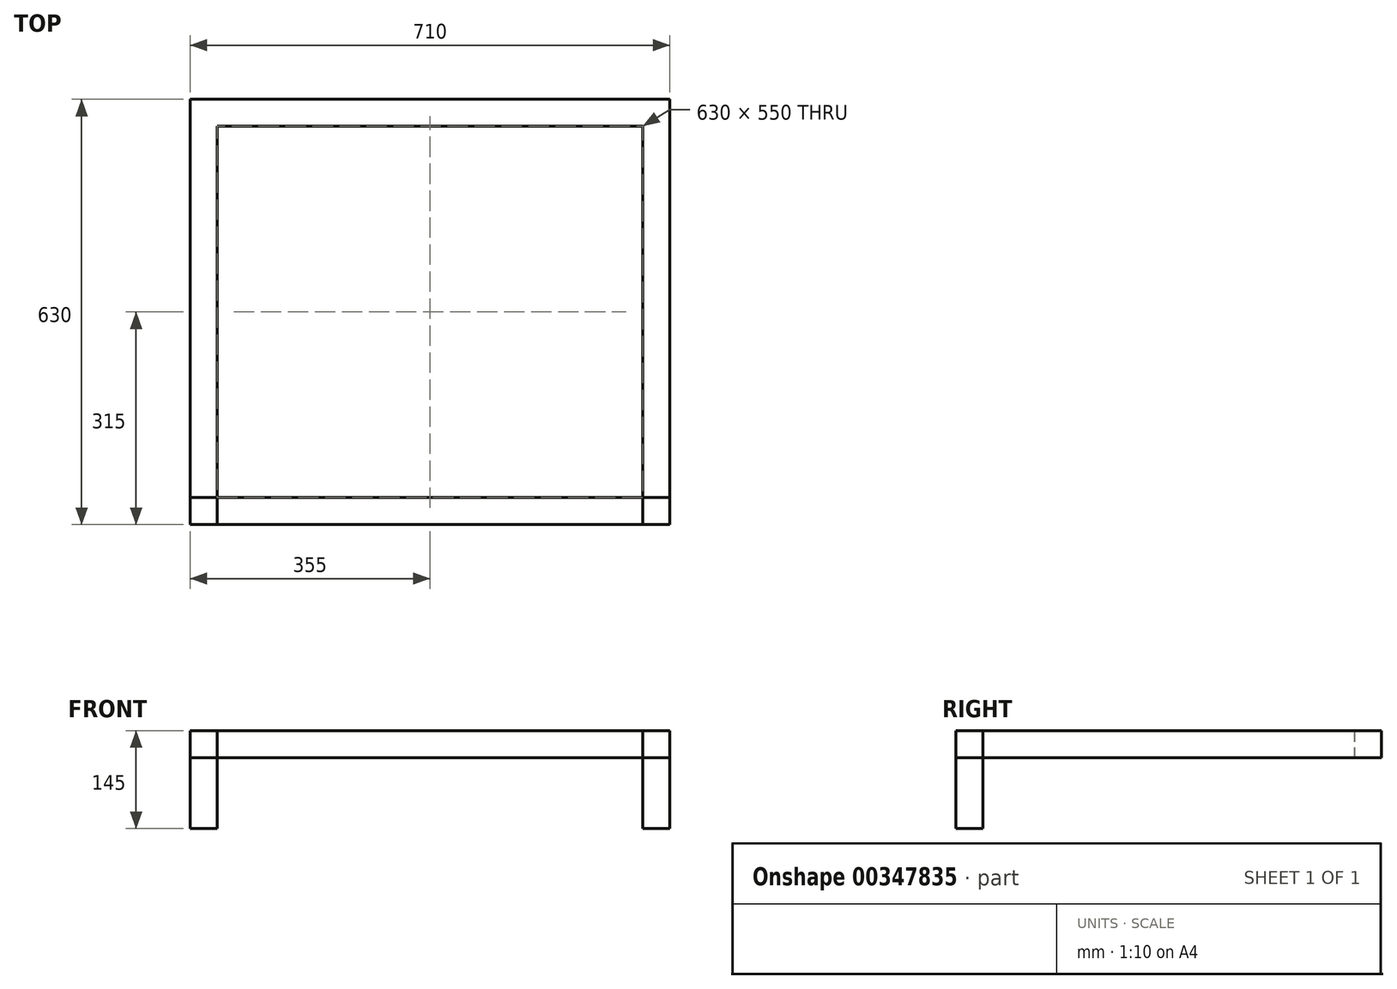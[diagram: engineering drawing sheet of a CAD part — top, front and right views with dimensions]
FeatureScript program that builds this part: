
annotation { "Feature Type Name" : "Feature", "Feature Type Description" : "" }
export const myFeature = defineFeature(function(context is Context, id is Id, definition is map)
    precondition{}
    {
        {
            var Q0;
            Q0=qCreatedBy(makeId("Top.planeOp"),FACE);
            var sketch = newSketch(context, id + "F0", { "sketchPlane" : qUnion([Q0])});
            skLineSegment(sketch, "E0.bottom", {"start": v(355, -315) * mm, "end": v(-355, -315) * mm});
            skLineSegment(sketch, "E0.top", {"start": v(355, 315) * mm, "end": v(-355, 315) * mm});
            skLineSegment(sketch, "E0.left", {"start": v(355, -315) * mm, "end": v(355, 315) * mm});
            skLineSegment(sketch, "E0.right", {"start": v(-355, -315) * mm, "end": v(-355, 315) * mm});
            skPoint(sketch, "E0.middle", {"position": v(0, 0) * mm});
            skLineSegment(sketch, "E1.0", {"start": v(315, 275) * mm, "end": v(-315, 275) * mm});
            skLineSegment(sketch, "E1.1", {"start": v(315, -275) * mm, "end": v(315, 275) * mm});
            skLineSegment(sketch, "E1.2", {"start": v(315, -275) * mm, "end": v(-315, -275) * mm});
            skLineSegment(sketch, "E1.3", {"start": v(-315, -275) * mm, "end": v(-315, 275) * mm});
            skLineSegment(sketch, "E2.bottom", {"start": v(-355, 315) * mm, "end": v(-315, 315) * mm});
            skLineSegment(sketch, "E2.top", {"start": v(-355, 275) * mm, "end": v(-315, 275) * mm});
            skLineSegment(sketch, "E2.left", {"start": v(-355, 315) * mm, "end": v(-355, 275) * mm});
            skLineSegment(sketch, "E2.right", {"start": v(-315, 315) * mm, "end": v(-315, 275) * mm});
            skLineSegment(sketch, "E3.bottom", {"start": v(355, 315) * mm, "end": v(315, 315) * mm});
            skLineSegment(sketch, "E3.top", {"start": v(355, 275) * mm, "end": v(315, 275) * mm});
            skLineSegment(sketch, "E3.left", {"start": v(355, 315) * mm, "end": v(355, 275) * mm});
            skLineSegment(sketch, "E3.right", {"start": v(315, 315) * mm, "end": v(315, 275) * mm});
            skLineSegment(sketch, "E4.bottom", {"start": v(315, -275) * mm, "end": v(355, -275) * mm});
            skLineSegment(sketch, "E4.top", {"start": v(315, -315) * mm, "end": v(355, -315) * mm});
            skLineSegment(sketch, "E4.left", {"start": v(315, -275) * mm, "end": v(315, -315) * mm});
            skLineSegment(sketch, "E4.right", {"start": v(355, -275) * mm, "end": v(355, -315) * mm});
            skLineSegment(sketch, "E5.bottom", {"start": v(-315, -275) * mm, "end": v(-355, -275) * mm});
            skLineSegment(sketch, "E5.top", {"start": v(-315, -315) * mm, "end": v(-355, -315) * mm});
            skLineSegment(sketch, "E5.left", {"start": v(-315, -275) * mm, "end": v(-315, -315) * mm});
            skLineSegment(sketch, "E5.right", {"start": v(-355, -275) * mm, "end": v(-355, -315) * mm});
            skSolve(sketch);
        }
        {
            var Q0;
            Q0=makeQuery(id+"F0.imprint","IMPRINT",FACE,{"disambiguationData":[TD([[makeQuery(id+"F0.imprint","IMPRINT",EDGE,{"derivedFrom":sQuery(id+"F0.wireOp",EDGE,"E2.bottom")}),-1.0]])]});
            var Q1;
            Q1=makeQuery(id+"F0.imprint","IMPRINT",FACE,{"disambiguationData":[TD([[makeQuery(id+"F0.imprint","IMPRINT",EDGE,{"derivedFrom":sQuery(id+"F0.wireOp",EDGE,"E3.bottom")}),1.0]])]});
            var Q2;
            Q2=makeQuery(id+"F0.imprint","IMPRINT",FACE,{"disambiguationData":[TD([[makeQuery(id+"F0.imprint","IMPRINT",EDGE,{"derivedFrom":sQuery(id+"F0.wireOp",EDGE,"E4.bottom")}),-1.0]])]});
            var Q3;
            Q3=makeQuery(id+"F0.imprint","IMPRINT",FACE,{"disambiguationData":[TD([[makeQuery(id+"F0.imprint","IMPRINT",EDGE,{"derivedFrom":sQuery(id+"F0.wireOp",EDGE,"E5.bottom")}),1.0]])]});
            extrude(context, id + "F1", {"entities" : qUnion([Q0, Q1, Q2, Q3]), "oppositeDirection" : true, "depth" : 145 * mm});
        }
        {
            var Q0;
            Q0=makeQuery(id+"F0.imprint","IMPRINT",FACE,{"disambiguationData":[TD([[makeQuery(id+"F0.imprint","IMPRINT",EDGE,{"derivedFrom":sQuery(id+"F0.wireOp",EDGE,"E0.bottom")}),-1.0]])]});
            var Q1;
            Q1=makeQuery(id+"F0.imprint","IMPRINT",FACE,{"disambiguationData":[TD([[makeQuery(id+"F0.imprint","IMPRINT",EDGE,{"derivedFrom":sQuery(id+"F0.wireOp",EDGE,"E0.left")}),1.0]])]});
            var Q2;
            Q2=makeQuery(id+"F0.imprint","IMPRINT",FACE,{"disambiguationData":[TD([[makeQuery(id+"F0.imprint","IMPRINT",EDGE,{"derivedFrom":sQuery(id+"F0.wireOp",EDGE,"E0.top")}),1.0]])]});
            var Q3;
            Q3=makeQuery(id+"F0.imprint","IMPRINT",FACE,{"disambiguationData":[TD([[makeQuery(id+"F0.imprint","IMPRINT",EDGE,{"derivedFrom":sQuery(id+"F0.wireOp",EDGE,"E0.right")}),-1.0]])]});
            extrude(context, id + "F2", {"entities" : qUnion([Q0, Q1, Q2, Q3]), "oppositeDirection" : true, "depth" : 40 * mm});
        }
    });
